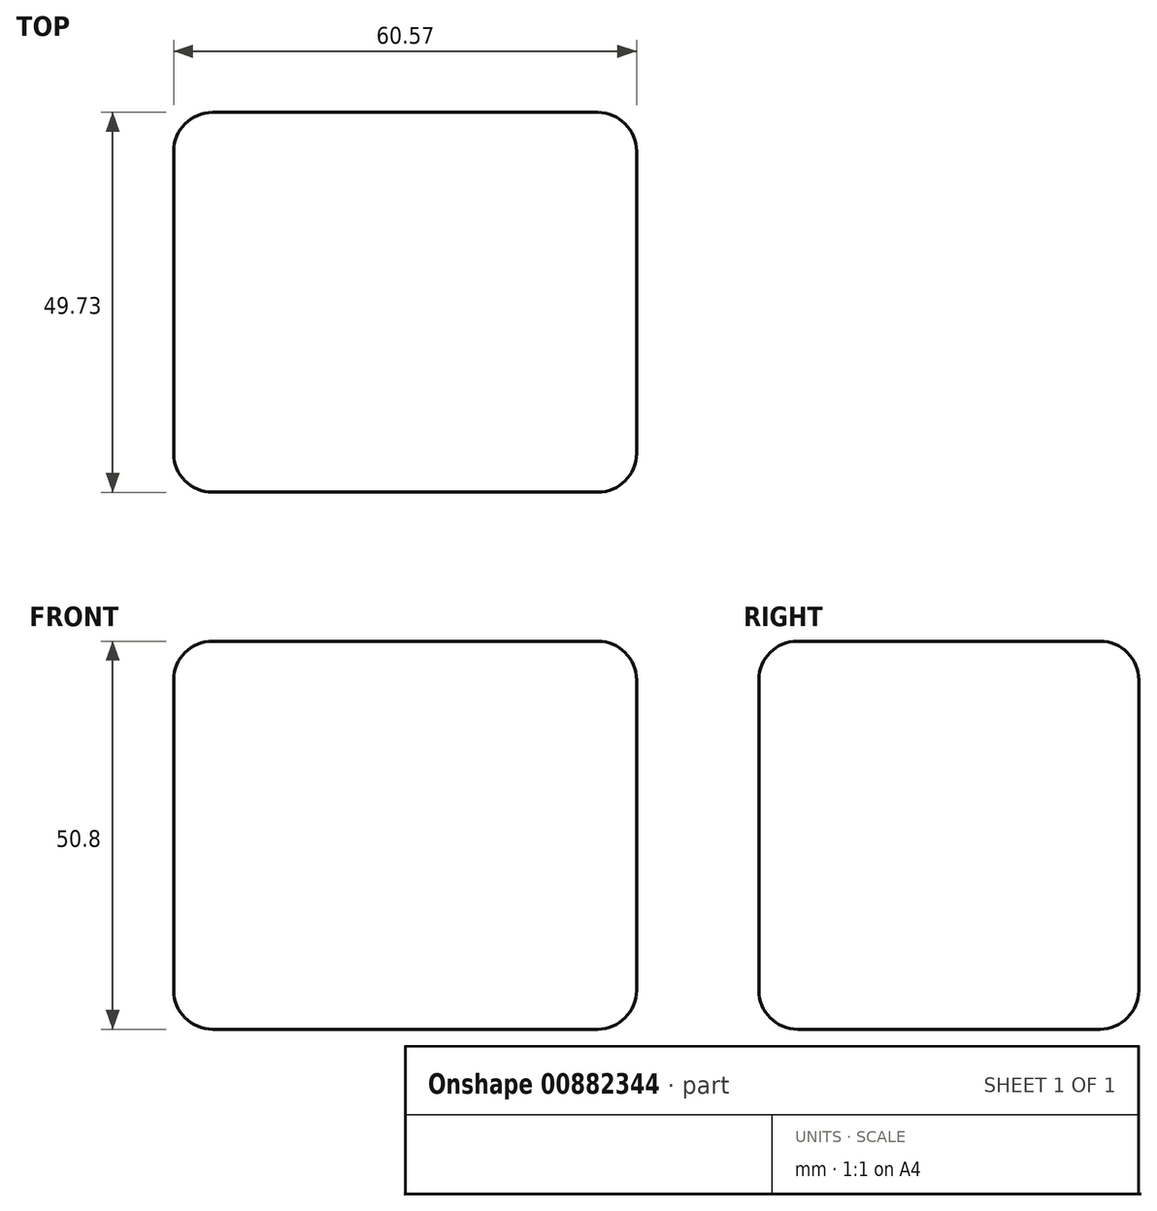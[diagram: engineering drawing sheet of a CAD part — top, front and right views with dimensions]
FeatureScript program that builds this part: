
annotation { "Feature Type Name" : "Feature", "Feature Type Description" : "" }
export const myFeature = defineFeature(function(context is Context, id is Id, definition is map)
    precondition{}
    {
        {
            var Q0;
            Q0=qCreatedBy(makeId("Top.planeOp"),FACE);
            var sketch = newSketch(context, id + "F0", { "sketchPlane" : qUnion([Q0])});
            skLineSegment(sketch, "E0.bottom", {"start": v(-26.45, 24.6) * mm, "end": v(34.12, 24.6) * mm});
            skLineSegment(sketch, "E0.top", {"start": v(-26.45, -25.13) * mm, "end": v(34.12, -25.13) * mm});
            skLineSegment(sketch, "E0.left", {"start": v(-26.45, 24.6) * mm, "end": v(-26.45, -25.13) * mm});
            skLineSegment(sketch, "E0.right", {"start": v(34.12, 24.6) * mm, "end": v(34.12, -25.13) * mm});
            skSolve(sketch);
        }
        {
            var Q0;
            Q0 = qSketchRegion(id + "F0", true);
            extrude(context, id + "F1", {"entities" : qUnion([Q0]), "depth" : 50.8 * mm, "offsetDistance" : 25.4 * mm});
        }
        {
            var Q0;
            Q0=makeQuery(id+"F1.opExtrude","CAP_EDGE",EDGE,{"disambiguationData":[OSD([sQuery(id+"F0.wireOp",EDGE,"E0.top")])],"isStart":false});
            var Q1;
            Q1=makeQuery(id+"F1.opExtrude","CAP_EDGE",EDGE,{"disambiguationData":[OSD([sQuery(id+"F0.wireOp",EDGE,"E0.left")])],"isStart":false});
            var Q2;
            Q2=makeQuery(id+"F1.opExtrude","CAP_EDGE",EDGE,{"disambiguationData":[OSD([sQuery(id+"F0.wireOp",EDGE,"E0.bottom")])],"isStart":false});
            var Q3;
            Q3=makeQuery(id+"F1.opExtrude","CAP_EDGE",EDGE,{"disambiguationData":[OSD([sQuery(id+"F0.wireOp",EDGE,"E0.right")])],"isStart":false});
            fillet(context, id + "F2", {"entities" : qUnion([Q0, Q1, Q2, Q3]), "radius" : 5.08 * mm, "tangentPropagation" : true, "allowEdgeOverflow" : false});
        }
        {
            var Q0;
            Q0=makeQuery(id+"F1.opExtrude","CAP_EDGE",EDGE,{"disambiguationData":[OSD([sQuery(id+"F0.wireOp",EDGE,"E0.top")])],"isStart":true});
            var Q1;
            Q1=makeQuery(id+"F1.opExtrude","CAP_EDGE",EDGE,{"disambiguationData":[OSD([sQuery(id+"F0.wireOp",EDGE,"E0.right")])],"isStart":true});
            var Q2;
            Q2=makeQuery(id+"F1.opExtrude","CAP_EDGE",EDGE,{"disambiguationData":[OSD([sQuery(id+"F0.wireOp",EDGE,"E0.bottom")])],"isStart":true});
            var Q3;
            Q3=makeQuery(id+"F1.opExtrude","CAP_EDGE",EDGE,{"disambiguationData":[OSD([sQuery(id+"F0.wireOp",EDGE,"E0.left")])],"isStart":true});
            fillet(context, id + "F3", {"entities" : qUnion([Q0, Q1, Q2, Q3]), "radius" : 5.08 * mm, "tangentPropagation" : true, "allowEdgeOverflow" : false});
        }
        {
            var Q0;
            Q0=makeQuery(id+"F1.opExtrude","SWEPT_EDGE",EDGE,{"disambiguationData":[OSD([sQuery(id+"F0.wireOp",EDGE,"E0.bottom"),sQuery(id+"F0.wireOp",EDGE,"E0.left")])]});
            var Q1;
            Q1=makeQuery(id+"F1.opExtrude","SWEPT_EDGE",EDGE,{"disambiguationData":[OSD([sQuery(id+"F0.wireOp",EDGE,"E0.top"),sQuery(id+"F0.wireOp",EDGE,"E0.left")])]});
            var Q2;
            Q2=makeQuery(id+"F1.opExtrude","SWEPT_EDGE",EDGE,{"disambiguationData":[OSD([sQuery(id+"F0.wireOp",EDGE,"E0.bottom"),sQuery(id+"F0.wireOp",EDGE,"E0.right")])]});
            var Q3;
            Q3=makeQuery(id+"F1.opExtrude","SWEPT_EDGE",EDGE,{"disambiguationData":[OSD([sQuery(id+"F0.wireOp",EDGE,"E0.top"),sQuery(id+"F0.wireOp",EDGE,"E0.right")])]});
            fillet(context, id + "F4", {"entities" : qUnion([Q0, Q1, Q2, Q3]), "radius" : 5.08 * mm, "tangentPropagation" : true, "allowEdgeOverflow" : false});
        }
    });
